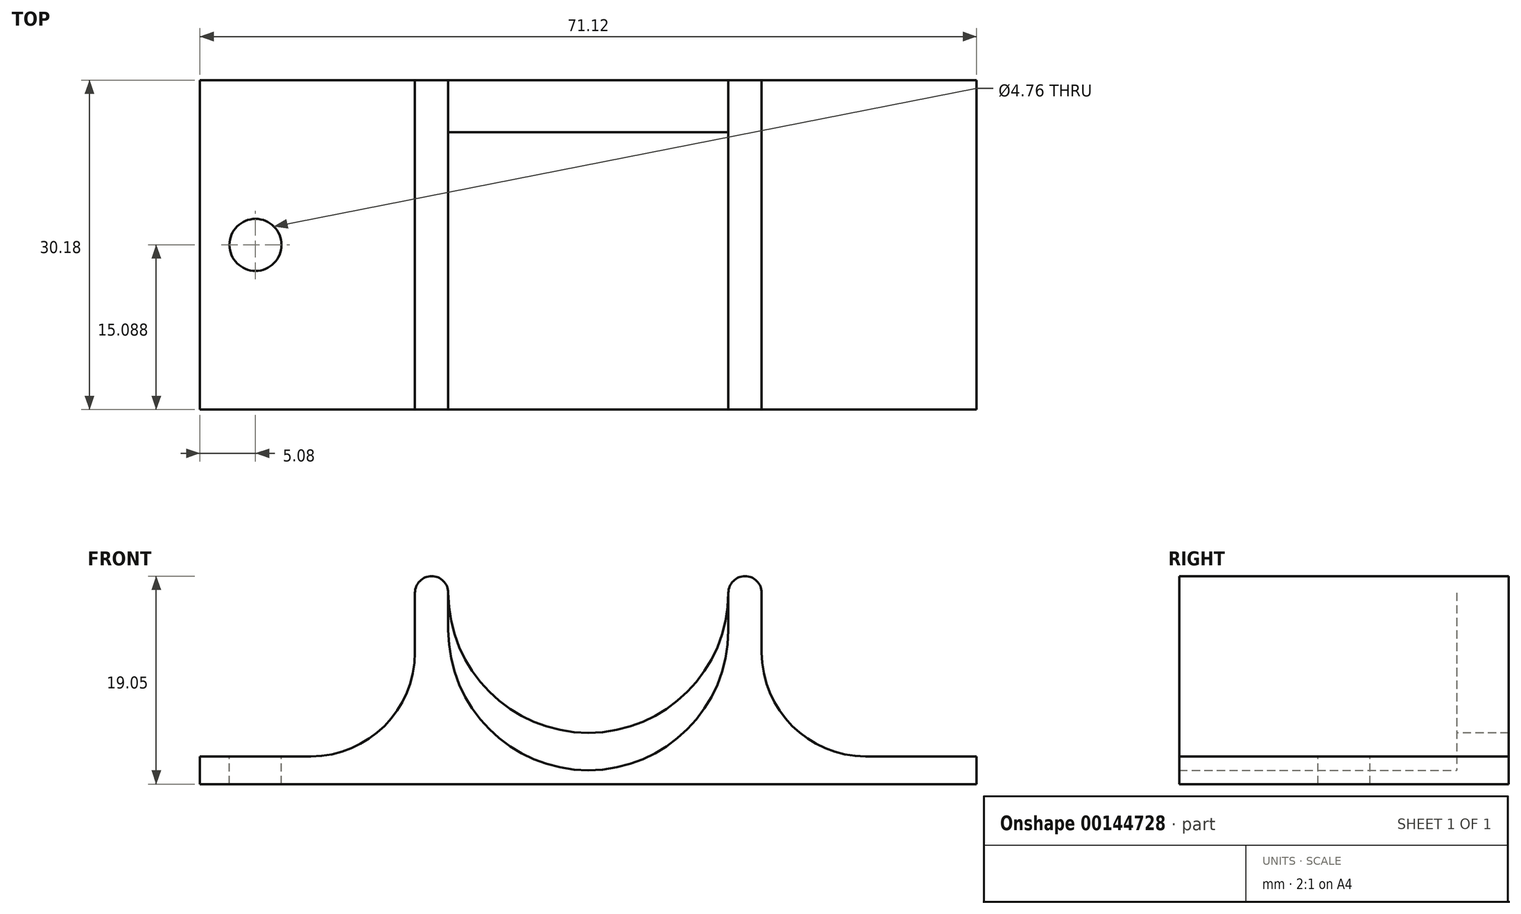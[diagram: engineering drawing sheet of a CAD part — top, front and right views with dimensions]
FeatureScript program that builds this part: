
annotation { "Feature Type Name" : "Feature", "Feature Type Description" : "" }
export const myFeature = defineFeature(function(context is Context, id is Id, definition is map)
    precondition{}
    {
        {
            var Q0;
            Q0=qCreatedBy(makeId("Front.planeOp"),FACE);
            var sketch = newSketch(context, id + "F0", { "sketchPlane" : qUnion([Q0])});
            skLineSegment(sketch, "E0.MirrorCS", {"start": v(0, 0) * mm, "end": v(-35.56, 0) * mm});
            skLineSegment(sketch, "E1.MirrorCS", {"start": v(-35.56, 0) * mm, "end": v(-35.56, 2.54) * mm});
            skLineSegment(sketch, "E2", {"start": v(-35.56, 2.54) * mm, "end": v(-25.4, 2.54) * mm});
            skArc(sketch, "E3", {"start": v(-15.88, 17.53) * mm, "mid": v(-14.35, 19.05) * mm, "end": v(-12.83, 17.53) * mm});
            skLineSegment(sketch, "E4", {"start": v(-12.83, 17.53) * mm, "end": v(-12.83, 14.1) * mm});
            skArc(sketch, "E5", {"start": v(-12.83, 14.1) * mm, "mid": v(-9.07, 5.03) * mm, "end": v(0, 1.27) * mm});
            skArc(sketch, "E6", {"start": v(-12.83, 17.53) * mm, "mid": v(-9.07, 8.46) * mm, "end": v(0, 4.7) * mm});
            skLineSegment(sketch, "E7", {"start": v(-15.88, 17.53) * mm, "end": v(-15.88, 12.06) * mm});
            skArc(sketch, "E8", {"start": v(-25.4, 2.54) * mm, "mid": v(-18.66, 5.33) * mm, "end": v(-15.88, 12.06) * mm});
            skLineSegment(sketch, "E9", {"start": v(0, 0) * mm, "end": v(0, 17.53) * mm, "construction": true});
            skLineSegment(sketch, "E10.MirrorCS", {"start": v(35.56, 0) * mm, "end": v(35.56, 2.54) * mm});
            skLineSegment(sketch, "E11.MirrorCS", {"start": v(15.88, 17.53) * mm, "end": v(15.88, 12.06) * mm});
            skArc(sketch, "E12.MirrorCS", {"start": v(12.83, 14.1) * mm, "mid": v(9.07, 5.03) * mm, "end": v(0, 1.27) * mm});
            skLineSegment(sketch, "E13.MirrorCS", {"start": v(0, 0) * mm, "end": v(35.56, 0) * mm});
            skArc(sketch, "E14.MirrorCS", {"start": v(12.83, 17.53) * mm, "mid": v(9.07, 8.46) * mm, "end": v(0, 4.7) * mm});
            skArc(sketch, "E15.MirrorCS", {"start": v(25.4, 2.54) * mm, "mid": v(18.66, 5.33) * mm, "end": v(15.88, 12.06) * mm});
            skArc(sketch, "E16.MirrorCS", {"start": v(15.88, 17.53) * mm, "mid": v(14.35, 19.05) * mm, "end": v(12.83, 17.53) * mm});
            skLineSegment(sketch, "E17.MirrorCS", {"start": v(35.56, 2.54) * mm, "end": v(25.4, 2.54) * mm});
            skLineSegment(sketch, "E18.MirrorCS", {"start": v(12.83, 17.53) * mm, "end": v(12.83, 14.1) * mm});
            skSolve(sketch);
        }
        {
            var Q0;
            Q0=makeQuery(id+"F0.imprint","IMPRINT",FACE,{"disambiguationData":[TD([[makeQuery(id+"F0.imprint","IMPRINT",EDGE,{"derivedFrom":sQuery(id+"F0.wireOp",EDGE,"E0.MirrorCS")}),-1.0]])]});
            extrude(context, id + "F1", {"entities" : qUnion([Q0]), "depth" : 25.4 * mm});
        }
        {
            var Q0;
            Q0 = qSketchRegion(id + "F0", true);
            extrude(context, id + "F2", {"entities" : qUnion([Q0]), "operationType" : NewBodyOperationType.ADD, "oppositeDirection" : true, "depth" : 4.78 * mm});
        }
        {
            var Q0;
            {var subQ0=sQuery(id+"F0.wireOp",EDGE,"E2");Q0=makeQuery(id+"F2.boolean.opBoolean","MERGE",FACE,{"derivedFrom":[makeQuery(id+"F1.opExtrude","SWEPT_FACE",FACE,{"disambiguationData":[OSD([subQ0])]}),makeQuery(id+"F2.opExtrude","SWEPT_FACE",FACE,{"disambiguationData":[OSD([subQ0])]})]});}
            var sketch = newSketch(context, id + "F3", { "sketchPlane" : qUnion([Q0])});
            skPoint(sketch, "E19", {"position": v(-30.48, 4.78) * mm});
            skPoint(sketch, "E20", {"position": v(-30.48, -25.4) * mm});
            skLineSegment(sketch, "E21", {"start": v(-30.48, 4.78) * mm, "end": v(-30.48, -25.4) * mm, "construction": true});
            skPoint(sketch, "E22", {"position": v(-30.48, -10.31) * mm});
            skSolve(sketch);
        }
        {
            var Q0;
            Q0=sQuery(id+"F3.wireOp",VERTEX,"E22");
            var Q1;
            Q1=makeQuery(id+"F1.opExtrude","SWEPT_BODY",BODY,{"disambiguationData":[OSD([sQuery(id+"F0.wireOp",EDGE,"E0.MirrorCS"),sQuery(id+"F0.wireOp",EDGE,"E1.MirrorCS"),sQuery(id+"F0.wireOp",EDGE,"E2"),sQuery(id+"F0.wireOp",EDGE,"E3"),sQuery(id+"F0.wireOp",EDGE,"E4"),sQuery(id+"F0.wireOp",EDGE,"E5"),sQuery(id+"F0.wireOp",EDGE,"E7"),sQuery(id+"F0.wireOp",EDGE,"E8"),sQuery(id+"F0.wireOp",EDGE,"bed7268b-c4e2-4a64-8d5d-7bedd126809f0.MirrorCS"),sQuery(id+"F0.wireOp",EDGE,"13f5c402-0cc7-4d11-9438-828886b22dba0.MirrorCS"),sQuery(id+"F0.wireOp",EDGE,"7293b2bd-52fe-41be-b4a8-a5cc158b19690.MirrorCS"),sQuery(id+"F0.wireOp",EDGE,"99893f9a-4ad7-43f4-a965-463063e4656d0.MirrorCS"),sQuery(id+"F0.wireOp",EDGE,"cb28e50a-d94c-4974-bf6c-410ef07eecf50.MirrorCS"),sQuery(id+"F0.wireOp",EDGE,"c9a15693-b0c8-4fb9-9adb-a3dce5f92d580.MirrorCS"),sQuery(id+"F0.wireOp",EDGE,"ef1bec6c-19d4-4a89-a2d5-c476ed9b68860.MirrorCS"),sQuery(id+"F0.wireOp",EDGE,"8c16247a-bf84-45b2-8fae-9c84c488bdee0.MirrorCS")])]});
            hole(context, id + "F4", {"style" : HoleStyle.SIMPLE, "endStyle" : HoleEndStyle.THROUGH, "holeDiameter" : 4.76 * mm, "locations" : qUnion([Q0]), "scope" : qUnion([Q1]), "isTappedThrough" : true});
        }
    });
